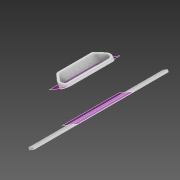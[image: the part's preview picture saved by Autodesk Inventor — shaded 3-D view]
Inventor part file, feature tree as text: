
AUTODESK INVENTOR PART (.ipt)
format: ipt  version: 2020 (Build 240168000, 168)  size: 500,224 bytes
history: native  units: in
note: dims shown in document units (in); Inventor stores cm internally (conversion verified against a paired STEP export)
features: extrude x8, sketch x8, fillet x4, plane x2, mirror x2, other x2, loft x1
ambient origin geometry x8: Origin, YZ Plane, XZ Plane, XY Plane, X Axis, Y Axis, Z Axis, Center Point
bodies: Solid1 (feature_tree)
feature tree (27):
  extrude  "Extrusion1"  Depth=0.3543in
  fillet  "Fillet1"  Radius=0.3543in
  fillet  "Fillet2"  Radius=1.0236in
  plane  "Work Plane1"
  extrude  "Extrusion2"  Depth=1.0236in
  fillet  "Fillet3"  Radius=1.6555in
  fillet  "Fillet4"  Radius=0.4724in
  loft  "Loft1"
  mirror  "Mirror4"
  extrude  "Extrusion3"  Depth=0.1181in
  extrude  "Extrusion4"  Depth=0.1181in
  extrude  "Extrusion5"  TaperAngle=0.0deg  [1 undecoded]
  extrude  "Extrusion6"  Depth=0.0787in TaperAngle=0.0deg
  extrude  "Extrusion7"  Depth=0.0787in
  plane  "Work Plane2"
  extrude  "Extrusion8"  TaperAngle=0.0deg  [1 undecoded]
  mirror  "Mirror5"
  sketch  "Sketch1"  dims[d0=0.3543in d1=0.3543in d2=0.3543in d3=1.0236in]
  sketch  "Sketch3"  dims[d4=90.0deg d5=1.0236in d7=1.6555in d9=0.4724in]
  other  "Edges1"
  other  "Edges2"
  sketch  "Sketch4"  dims[d10=0.9449in d17=0.0394in d18=0.0in]
  sketch  "Sketch5"  dims[d19=0.1969in d21=0.1181in]
  sketch  "Sketch6"  dims[d22=0.315in d23=0.1181in]
  sketch  "Sketch7"  dims[d24=30.0deg d35=0.0in]
  sketch  "Sketch8"  dims[d36=0.1181in d37=0.0787in d38=0.0in]
  sketch  "Sketch10"  dims[d39=0.1969in d40=0.315in d41=0.0in d42=90.0deg d43=0.0in d44=90.0deg d45=0.0787in d46=0.0in d47=0.0394in d48=0.0in d49=0.0394in d50=0.0in d51=0.0394in d52=0.0in d53=0.0394in d54=0.0in d55=1.5748in d56=3.937in d57=0.0787in d58=0.1575in d59=0.0787in d60=0.0787in d61=0.315in d62=0.1181in d63=0.0in]
note: 2 required parameter values undecoded (feature->parameter linkage not recoverable at this tier; creation-order binding heuristic only, values carry confidence <= 0.55)
